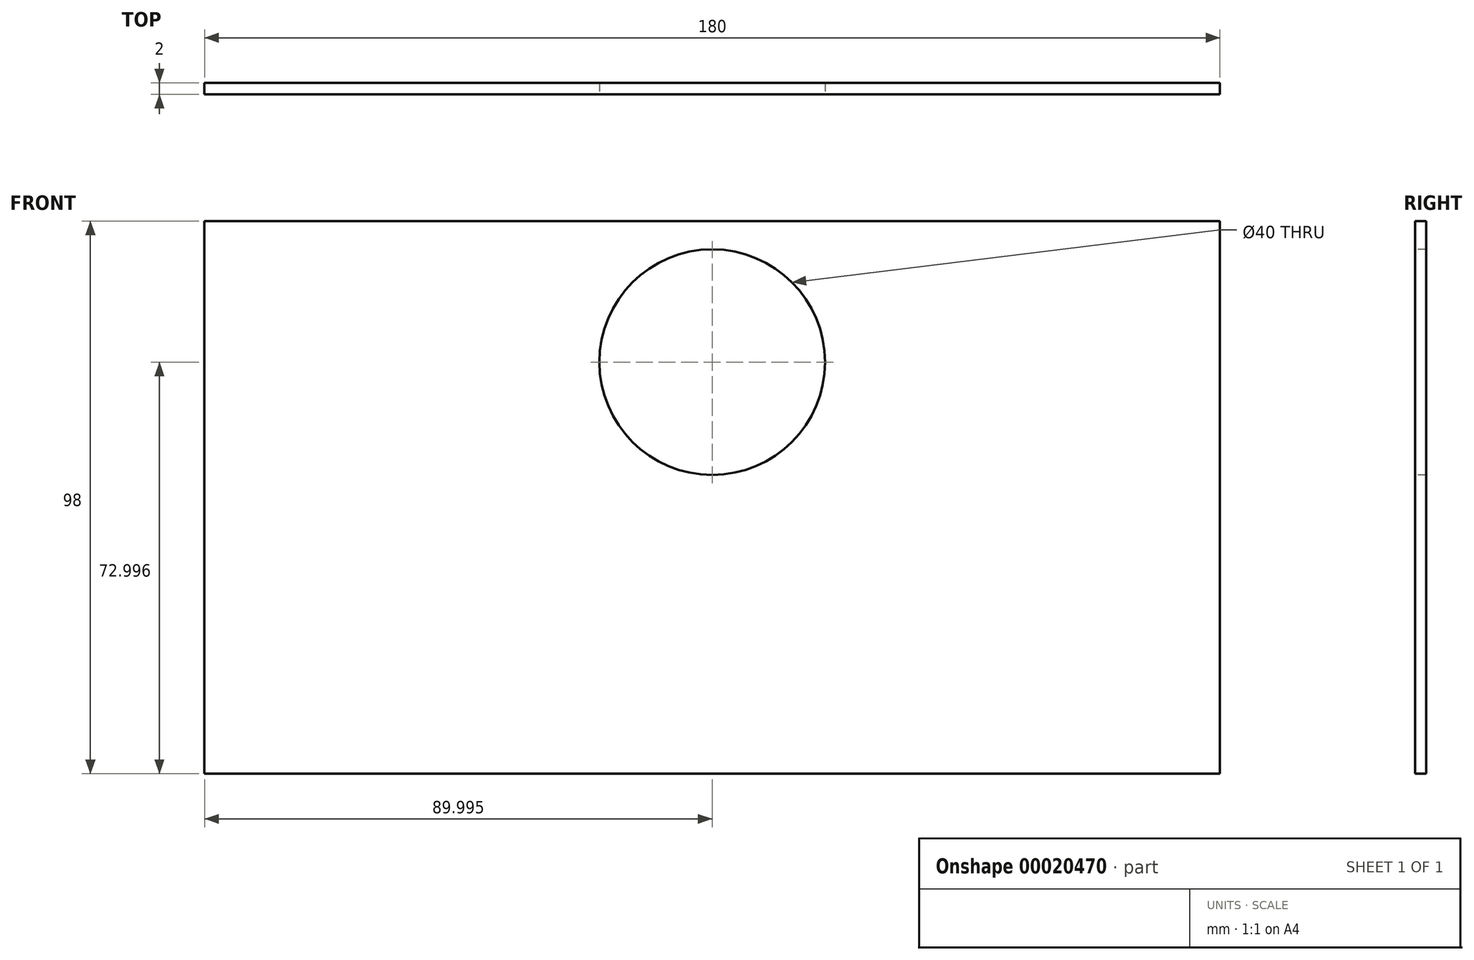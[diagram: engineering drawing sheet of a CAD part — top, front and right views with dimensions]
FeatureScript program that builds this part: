
annotation { "Feature Type Name" : "Feature", "Feature Type Description" : "" }
export const myFeature = defineFeature(function(context is Context, id is Id, definition is map)
    precondition{}
    {
        {
            var Q0;
            Q0=qCreatedBy(makeId("Front.planeOp"),FACE);
            var sketch = newSketch(context, id + "F0", { "sketchPlane" : qUnion([Q0])});
            skLineSegment(sketch, "E0.bottom", {"start": v(-84.4, 43.33) * mm, "end": v(95.6, 43.33) * mm});
            skLineSegment(sketch, "E0.top", {"start": v(-84.4, -54.67) * mm, "end": v(95.6, -54.67) * mm});
            skLineSegment(sketch, "E0.left", {"start": v(-84.4, 43.33) * mm, "end": v(-84.4, -54.67) * mm});
            skLineSegment(sketch, "E0.right", {"start": v(95.6, 43.33) * mm, "end": v(95.6, -54.67) * mm});
            skCircle(sketch, "E1", {"center": v(5.6, 18.33) * mm, "radius": 20 * mm});
            skSolve(sketch);
        }
        {
            var Q0;
            Q0=makeQuery(id+"F0.imprint","IMPRINT",FACE,{"disambiguationData":[TD([[makeQuery(id+"F0.imprint","IMPRINT",EDGE,{"derivedFrom":sQuery(id+"F0.wireOp",EDGE,"E0.bottom")}),-1.0]])]});
            extrude(context, id + "F1", {"entities" : qUnion([Q0]), "oppositeDirection" : true, "depth" : 2 * mm});
        }
    });
